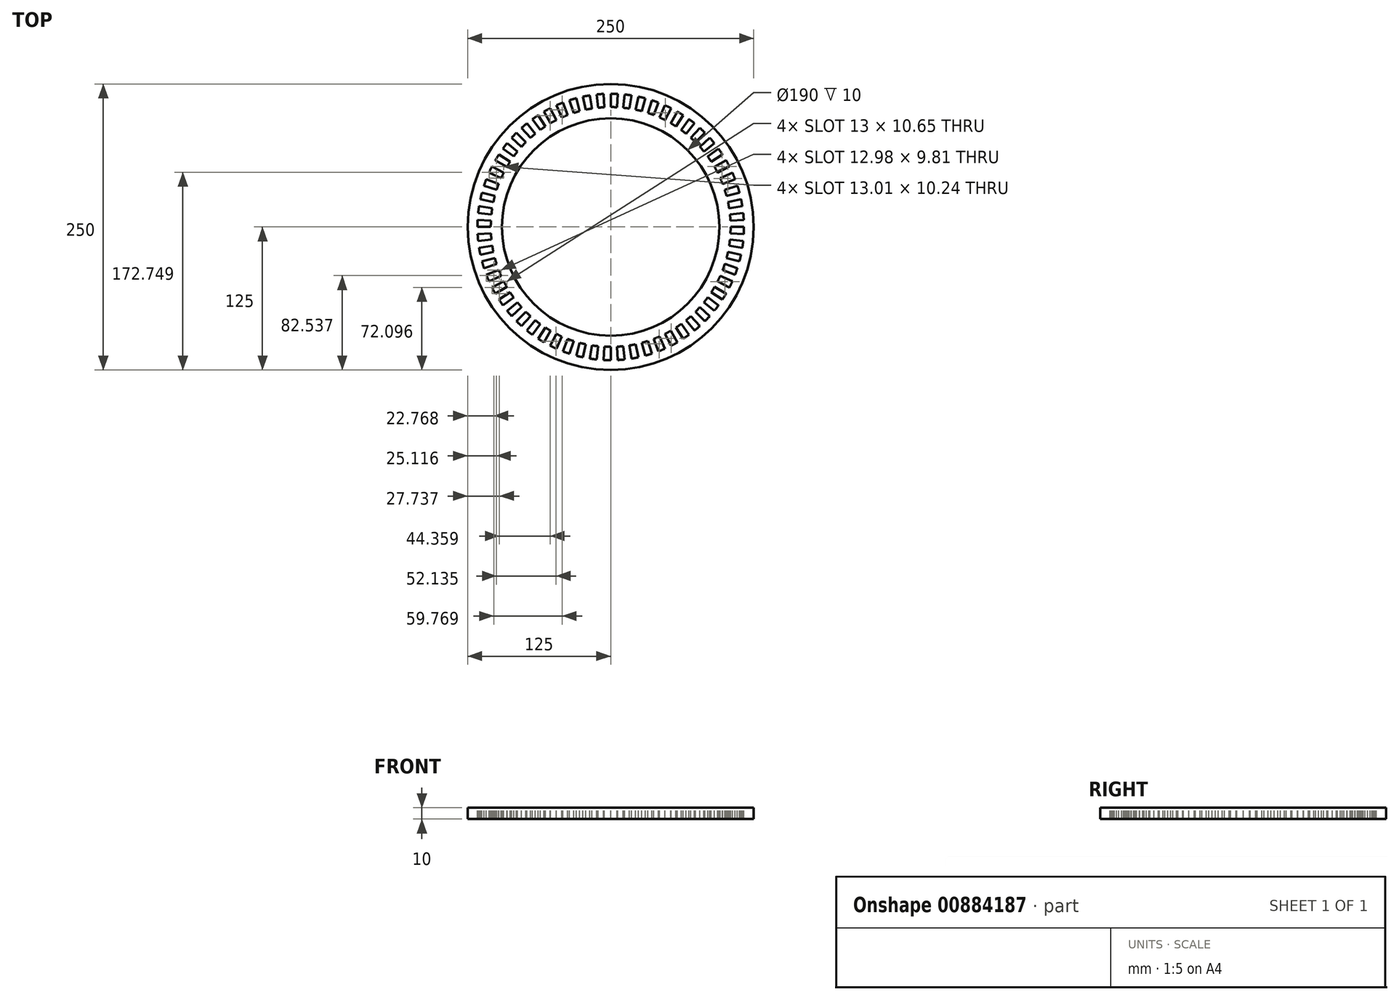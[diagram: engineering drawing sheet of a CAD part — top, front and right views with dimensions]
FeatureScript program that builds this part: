
annotation { "Feature Type Name" : "Feature", "Feature Type Description" : "" }
export const myFeature = defineFeature(function(context is Context, id is Id, definition is map)
    precondition{}
    {
        {
            var Q0;
            Q0=qCreatedBy(makeId("Top.planeOp"),FACE);
            var sketch = newSketch(context, id + "F0", { "sketchPlane" : qUnion([Q0])});
            skCircle(sketch, "E0", {"center": v(0, 0) * mm, "radius": 145 * mm});
            skArc(sketch, "E1", {"start": v(9.54, 136.41) * mm, "mid": v(4.77, 136.66) * mm, "end": v(0, 136.75) * mm});
            skArc(sketch, "E2", {"start": v(8, 114.55) * mm, "mid": v(4, 114.76) * mm, "end": v(0, 114.83) * mm});
            skLineSegment(sketch, "E3", {"start": v(0, 0) * mm, "end": v(0, 38.61) * mm, "construction": true});
            skLineSegment(sketch, "E4", {"start": v(0, 38.61) * mm, "end": v(0, 0) * mm, "construction": true});
            skLineSegment(sketch, "E5", {"start": v(0, 0) * mm, "end": v(-47.77, 0) * mm, "construction": true});
            skLineSegment(sketch, "E6", {"start": v(0, 30) * mm, "end": v(-10, 30) * mm});
            skLineSegment(sketch, "E7", {"start": v(-10, 30) * mm, "end": v(-10, 10) * mm});
            skLineSegment(sketch, "E8", {"start": v(-10, 10) * mm, "end": v(-30, 10) * mm});
            skLineSegment(sketch, "E9", {"start": v(-30, 10) * mm, "end": v(-30, 0) * mm});
            skLineSegment(sketch, "E10.MirrorCS", {"start": v(-30, -10) * mm, "end": v(-30, 0) * mm});
            skLineSegment(sketch, "E11.MirrorCS", {"start": v(-10, -10) * mm, "end": v(-30, -10) * mm});
            skLineSegment(sketch, "E12.MirrorCS", {"start": v(-10, -30) * mm, "end": v(-10, -10) * mm});
            skLineSegment(sketch, "E13.MirrorCS", {"start": v(0, -30) * mm, "end": v(-10, -30) * mm});
            skLineSegment(sketch, "E14.MirrorCS", {"start": v(0, 30) * mm, "end": v(10, 30) * mm});
            skLineSegment(sketch, "E15.MirrorCS", {"start": v(10, 30) * mm, "end": v(10, 10) * mm});
            skLineSegment(sketch, "E16.MirrorCS", {"start": v(10, 10) * mm, "end": v(30, 10) * mm});
            skLineSegment(sketch, "E17.MirrorCS", {"start": v(30, 10) * mm, "end": v(30, 0) * mm});
            skLineSegment(sketch, "E18.MirrorCS", {"start": v(30, -10) * mm, "end": v(30, 0) * mm});
            skLineSegment(sketch, "E19.MirrorCS", {"start": v(10, -10) * mm, "end": v(30, -10) * mm});
            skLineSegment(sketch, "E20.MirrorCS", {"start": v(0, -30) * mm, "end": v(10, -30) * mm});
            skLineSegment(sketch, "E21.MirrorCS", {"start": v(10, -30) * mm, "end": v(10, -10) * mm});
            skLineSegment(sketch, "E22", {"start": v(0, 114.83) * mm, "end": v(0, 136.75) * mm});
            skLineSegment(sketch, "E23", {"start": v(8, 114.55) * mm, "end": v(9.54, 136.41) * mm});
            skArc(sketch, "E24.1.0", {"start": v(-10, 114.4) * mm, "mid": v(-14, 113.98) * mm, "end": v(-17.96, 113.42) * mm});
            skLineSegment(sketch, "E24.1.1", {"start": v(-17.96, 113.42) * mm, "end": v(-21.4, 135.06) * mm});
            skArc(sketch, "E24.1.2", {"start": v(-11.92, 136.23) * mm, "mid": v(-16.67, 135.73) * mm, "end": v(-21.4, 135.06) * mm});
            skLineSegment(sketch, "E24.1.3", {"start": v(-10, 114.4) * mm, "end": v(-11.92, 136.23) * mm});
            skArc(sketch, "E24.2.0", {"start": v(-27.78, 111.42) * mm, "mid": v(-31.65, 110.39) * mm, "end": v(-35.49, 109.21) * mm});
            skLineSegment(sketch, "E24.2.1", {"start": v(-35.49, 109.21) * mm, "end": v(-42.26, 130.05) * mm});
            skArc(sketch, "E24.2.2", {"start": v(-33.08, 132.68) * mm, "mid": v(-37.7, 131.45) * mm, "end": v(-42.26, 130.05) * mm});
            skLineSegment(sketch, "E24.2.3", {"start": v(-27.78, 111.42) * mm, "end": v(-33.08, 132.68) * mm});
            skArc(sketch, "E24.3.0", {"start": v(-44.87, 105.7) * mm, "mid": v(-48.53, 104.07) * mm, "end": v(-52.13, 102.32) * mm});
            skLineSegment(sketch, "E24.3.1", {"start": v(-52.13, 102.32) * mm, "end": v(-62.08, 121.84) * mm});
            skArc(sketch, "E24.3.2", {"start": v(-53.43, 125.88) * mm, "mid": v(-57.8, 123.93) * mm, "end": v(-62.08, 121.84) * mm});
            skLineSegment(sketch, "E24.3.3", {"start": v(-44.87, 105.7) * mm, "end": v(-53.43, 125.88) * mm});
            skArc(sketch, "E24.4.0", {"start": v(-60.85, 97.38) * mm, "mid": v(-64.21, 95.2) * mm, "end": v(-67.5, 92.9) * mm});
            skLineSegment(sketch, "E24.4.1", {"start": v(-67.5, 92.9) * mm, "end": v(-80.38, 110.63) * mm});
            skArc(sketch, "E24.4.2", {"start": v(-72.47, 115.97) * mm, "mid": v(-76.47, 113.37) * mm, "end": v(-80.38, 110.63) * mm});
            skLineSegment(sketch, "E24.4.3", {"start": v(-60.85, 97.38) * mm, "end": v(-72.47, 115.97) * mm});
            skArc(sketch, "E24.5.0", {"start": v(-75.34, 86.67) * mm, "mid": v(-78.32, 83.98) * mm, "end": v(-81.2, 81.2) * mm});
            skLineSegment(sketch, "E24.5.1", {"start": v(-81.2, 81.2) * mm, "end": v(-96.7, 96.7) * mm});
            skArc(sketch, "E24.5.2", {"start": v(-89.71, 103.2) * mm, "mid": v(-93.26, 100.01) * mm, "end": v(-96.7, 96.7) * mm});
            skLineSegment(sketch, "E24.5.3", {"start": v(-75.34, 86.67) * mm, "end": v(-89.71, 103.2) * mm});
            skArc(sketch, "E24.6.0", {"start": v(-87.97, 73.81) * mm, "mid": v(-90.5, 70.7) * mm, "end": v(-92.9, 67.5) * mm});
            skLineSegment(sketch, "E24.6.1", {"start": v(-92.9, 67.5) * mm, "end": v(-110.63, 80.38) * mm});
            skArc(sketch, "E24.6.2", {"start": v(-104.75, 87.9) * mm, "mid": v(-107.76, 84.19) * mm, "end": v(-110.63, 80.38) * mm});
            skLineSegment(sketch, "E24.6.3", {"start": v(-87.97, 73.81) * mm, "end": v(-104.75, 87.9) * mm});
            skArc(sketch, "E24.7.0", {"start": v(-98.43, 59.14) * mm, "mid": v(-100.44, 55.67) * mm, "end": v(-102.32, 52.13) * mm});
            skLineSegment(sketch, "E24.7.1", {"start": v(-102.32, 52.13) * mm, "end": v(-121.84, 62.08) * mm});
            skArc(sketch, "E24.7.2", {"start": v(-117.22, 70.43) * mm, "mid": v(-119.6, 66.3) * mm, "end": v(-121.84, 62.08) * mm});
            skLineSegment(sketch, "E24.7.3", {"start": v(-98.43, 59.14) * mm, "end": v(-117.22, 70.43) * mm});
            skArc(sketch, "E24.8.0", {"start": v(-106.47, 43.02) * mm, "mid": v(-107.9, 39.28) * mm, "end": v(-109.21, 35.49) * mm});
            skLineSegment(sketch, "E24.8.1", {"start": v(-109.21, 35.49) * mm, "end": v(-130.05, 42.26) * mm});
            skArc(sketch, "E24.8.2", {"start": v(-126.79, 51.23) * mm, "mid": v(-128.5, 46.77) * mm, "end": v(-130.05, 42.26) * mm});
            skLineSegment(sketch, "E24.8.3", {"start": v(-106.47, 43.02) * mm, "end": v(-126.79, 51.23) * mm});
            skArc(sketch, "E24.9.0", {"start": v(-111.9, 25.83) * mm, "mid": v(-112.72, 21.91) * mm, "end": v(-113.42, 17.96) * mm});
            skLineSegment(sketch, "E24.9.1", {"start": v(-113.42, 17.96) * mm, "end": v(-135.06, 21.4) * mm});
            skArc(sketch, "E24.9.2", {"start": v(-133.24, 30.76) * mm, "mid": v(-134.23, 26.1) * mm, "end": v(-135.06, 21.4) * mm});
            skLineSegment(sketch, "E24.9.3", {"start": v(-111.9, 25.83) * mm, "end": v(-133.24, 30.76) * mm});
            skArc(sketch, "E24.10.0", {"start": v(-114.55, 8) * mm, "mid": v(-114.76, 4) * mm, "end": v(-114.83, 0) * mm});
            skLineSegment(sketch, "E24.10.1", {"start": v(-114.83, 0) * mm, "end": v(-136.75, 0) * mm});
            skArc(sketch, "E24.10.2", {"start": v(-136.41, 9.54) * mm, "mid": v(-136.66, 4.77) * mm, "end": v(-136.75, 0) * mm});
            skLineSegment(sketch, "E24.10.3", {"start": v(-114.55, 8) * mm, "end": v(-136.41, 9.54) * mm});
            skArc(sketch, "E24.11.0", {"start": v(-114.4, -10) * mm, "mid": v(-113.98, -14) * mm, "end": v(-113.42, -17.96) * mm});
            skLineSegment(sketch, "E24.11.1", {"start": v(-113.42, -17.96) * mm, "end": v(-135.06, -21.4) * mm});
            skArc(sketch, "E24.11.2", {"start": v(-136.23, -11.92) * mm, "mid": v(-135.73, -16.67) * mm, "end": v(-135.06, -21.4) * mm});
            skLineSegment(sketch, "E24.11.3", {"start": v(-114.4, -10) * mm, "end": v(-136.23, -11.92) * mm});
            skArc(sketch, "E24.12.0", {"start": v(-111.42, -27.78) * mm, "mid": v(-110.39, -31.65) * mm, "end": v(-109.21, -35.49) * mm});
            skLineSegment(sketch, "E24.12.1", {"start": v(-109.21, -35.49) * mm, "end": v(-130.05, -42.26) * mm});
            skArc(sketch, "E24.12.2", {"start": v(-132.68, -33.08) * mm, "mid": v(-131.45, -37.7) * mm, "end": v(-130.05, -42.26) * mm});
            skLineSegment(sketch, "E24.12.3", {"start": v(-111.42, -27.78) * mm, "end": v(-132.68, -33.08) * mm});
            skArc(sketch, "E24.13.0", {"start": v(-105.7, -44.87) * mm, "mid": v(-104.07, -48.53) * mm, "end": v(-102.32, -52.13) * mm});
            skLineSegment(sketch, "E24.13.1", {"start": v(-102.32, -52.13) * mm, "end": v(-121.84, -62.08) * mm});
            skArc(sketch, "E24.13.2", {"start": v(-125.88, -53.43) * mm, "mid": v(-123.93, -57.8) * mm, "end": v(-121.84, -62.08) * mm});
            skLineSegment(sketch, "E24.13.3", {"start": v(-105.7, -44.87) * mm, "end": v(-125.88, -53.43) * mm});
            skArc(sketch, "E24.14.0", {"start": v(-97.38, -60.85) * mm, "mid": v(-95.2, -64.21) * mm, "end": v(-92.9, -67.5) * mm});
            skLineSegment(sketch, "E24.14.1", {"start": v(-92.9, -67.5) * mm, "end": v(-110.63, -80.38) * mm});
            skArc(sketch, "E24.14.2", {"start": v(-115.97, -72.47) * mm, "mid": v(-113.37, -76.47) * mm, "end": v(-110.63, -80.38) * mm});
            skLineSegment(sketch, "E24.14.3", {"start": v(-97.38, -60.85) * mm, "end": v(-115.97, -72.47) * mm});
            skArc(sketch, "E24.15.0", {"start": v(-86.67, -75.34) * mm, "mid": v(-83.98, -78.32) * mm, "end": v(-81.2, -81.2) * mm});
            skLineSegment(sketch, "E24.15.1", {"start": v(-81.2, -81.2) * mm, "end": v(-96.7, -96.7) * mm});
            skArc(sketch, "E24.15.2", {"start": v(-103.2, -89.71) * mm, "mid": v(-100.01, -93.26) * mm, "end": v(-96.7, -96.7) * mm});
            skLineSegment(sketch, "E24.15.3", {"start": v(-86.67, -75.34) * mm, "end": v(-103.2, -89.71) * mm});
            skArc(sketch, "E24.16.0", {"start": v(-73.81, -87.97) * mm, "mid": v(-70.7, -90.5) * mm, "end": v(-67.5, -92.9) * mm});
            skLineSegment(sketch, "E24.16.1", {"start": v(-67.5, -92.9) * mm, "end": v(-80.38, -110.63) * mm});
            skArc(sketch, "E24.16.2", {"start": v(-87.9, -104.75) * mm, "mid": v(-84.19, -107.76) * mm, "end": v(-80.38, -110.63) * mm});
            skLineSegment(sketch, "E24.16.3", {"start": v(-73.81, -87.97) * mm, "end": v(-87.9, -104.75) * mm});
            skArc(sketch, "E24.17.0", {"start": v(-59.14, -98.43) * mm, "mid": v(-55.67, -100.44) * mm, "end": v(-52.13, -102.32) * mm});
            skLineSegment(sketch, "E24.17.1", {"start": v(-52.13, -102.32) * mm, "end": v(-62.08, -121.84) * mm});
            skArc(sketch, "E24.17.2", {"start": v(-70.43, -117.22) * mm, "mid": v(-66.3, -119.6) * mm, "end": v(-62.08, -121.84) * mm});
            skLineSegment(sketch, "E24.17.3", {"start": v(-59.14, -98.43) * mm, "end": v(-70.43, -117.22) * mm});
            skArc(sketch, "E24.18.0", {"start": v(-43.02, -106.47) * mm, "mid": v(-39.28, -107.9) * mm, "end": v(-35.49, -109.21) * mm});
            skLineSegment(sketch, "E24.18.1", {"start": v(-35.49, -109.21) * mm, "end": v(-42.26, -130.05) * mm});
            skArc(sketch, "E24.18.2", {"start": v(-51.23, -126.79) * mm, "mid": v(-46.77, -128.5) * mm, "end": v(-42.26, -130.05) * mm});
            skLineSegment(sketch, "E24.18.3", {"start": v(-43.02, -106.47) * mm, "end": v(-51.23, -126.79) * mm});
            skArc(sketch, "E24.19.0", {"start": v(-25.83, -111.9) * mm, "mid": v(-21.91, -112.72) * mm, "end": v(-17.96, -113.42) * mm});
            skLineSegment(sketch, "E24.19.1", {"start": v(-17.96, -113.42) * mm, "end": v(-21.4, -135.06) * mm});
            skArc(sketch, "E24.19.2", {"start": v(-30.76, -133.24) * mm, "mid": v(-26.1, -134.23) * mm, "end": v(-21.4, -135.06) * mm});
            skLineSegment(sketch, "E24.19.3", {"start": v(-25.83, -111.9) * mm, "end": v(-30.76, -133.24) * mm});
            skArc(sketch, "E24.20.0", {"start": v(-8, -114.55) * mm, "mid": v(-4, -114.76) * mm, "end": v(0, -114.83) * mm});
            skLineSegment(sketch, "E24.20.1", {"start": v(0, -114.83) * mm, "end": v(0, -136.75) * mm});
            skArc(sketch, "E24.20.2", {"start": v(-9.54, -136.41) * mm, "mid": v(-4.77, -136.66) * mm, "end": v(0, -136.75) * mm});
            skLineSegment(sketch, "E24.20.3", {"start": v(-8, -114.55) * mm, "end": v(-9.54, -136.41) * mm});
            skArc(sketch, "E24.21.0", {"start": v(10, -114.4) * mm, "mid": v(14, -113.98) * mm, "end": v(17.96, -113.42) * mm});
            skLineSegment(sketch, "E24.21.1", {"start": v(17.96, -113.42) * mm, "end": v(21.4, -135.06) * mm});
            skArc(sketch, "E24.21.2", {"start": v(11.92, -136.23) * mm, "mid": v(16.67, -135.73) * mm, "end": v(21.4, -135.06) * mm});
            skLineSegment(sketch, "E24.21.3", {"start": v(10, -114.4) * mm, "end": v(11.92, -136.23) * mm});
            skArc(sketch, "E24.22.0", {"start": v(27.78, -111.42) * mm, "mid": v(31.65, -110.39) * mm, "end": v(35.49, -109.21) * mm});
            skLineSegment(sketch, "E24.22.1", {"start": v(35.49, -109.21) * mm, "end": v(42.26, -130.05) * mm});
            skArc(sketch, "E24.22.2", {"start": v(33.08, -132.68) * mm, "mid": v(37.7, -131.45) * mm, "end": v(42.26, -130.05) * mm});
            skLineSegment(sketch, "E24.22.3", {"start": v(27.78, -111.42) * mm, "end": v(33.08, -132.68) * mm});
            skArc(sketch, "E24.23.0", {"start": v(44.87, -105.7) * mm, "mid": v(48.53, -104.07) * mm, "end": v(52.13, -102.32) * mm});
            skLineSegment(sketch, "E24.23.1", {"start": v(52.13, -102.32) * mm, "end": v(62.08, -121.84) * mm});
            skArc(sketch, "E24.23.2", {"start": v(53.43, -125.88) * mm, "mid": v(57.8, -123.93) * mm, "end": v(62.08, -121.84) * mm});
            skLineSegment(sketch, "E24.23.3", {"start": v(44.87, -105.7) * mm, "end": v(53.43, -125.88) * mm});
            skArc(sketch, "E24.24.0", {"start": v(60.85, -97.38) * mm, "mid": v(64.21, -95.2) * mm, "end": v(67.5, -92.9) * mm});
            skLineSegment(sketch, "E24.24.1", {"start": v(67.5, -92.9) * mm, "end": v(80.38, -110.63) * mm});
            skArc(sketch, "E24.24.2", {"start": v(72.47, -115.97) * mm, "mid": v(76.47, -113.37) * mm, "end": v(80.38, -110.63) * mm});
            skLineSegment(sketch, "E24.24.3", {"start": v(60.85, -97.38) * mm, "end": v(72.47, -115.97) * mm});
            skArc(sketch, "E24.25.0", {"start": v(75.34, -86.67) * mm, "mid": v(78.32, -83.98) * mm, "end": v(81.2, -81.2) * mm});
            skLineSegment(sketch, "E24.25.1", {"start": v(81.2, -81.2) * mm, "end": v(96.7, -96.7) * mm});
            skArc(sketch, "E24.25.2", {"start": v(89.71, -103.2) * mm, "mid": v(93.26, -100.01) * mm, "end": v(96.7, -96.7) * mm});
            skLineSegment(sketch, "E24.25.3", {"start": v(75.34, -86.67) * mm, "end": v(89.71, -103.2) * mm});
            skArc(sketch, "E24.26.0", {"start": v(87.97, -73.81) * mm, "mid": v(90.5, -70.7) * mm, "end": v(92.9, -67.5) * mm});
            skLineSegment(sketch, "E24.26.1", {"start": v(92.9, -67.5) * mm, "end": v(110.63, -80.38) * mm});
            skArc(sketch, "E24.26.2", {"start": v(104.75, -87.9) * mm, "mid": v(107.76, -84.19) * mm, "end": v(110.63, -80.38) * mm});
            skLineSegment(sketch, "E24.26.3", {"start": v(87.97, -73.81) * mm, "end": v(104.75, -87.9) * mm});
            skArc(sketch, "E24.27.0", {"start": v(98.43, -59.14) * mm, "mid": v(100.44, -55.67) * mm, "end": v(102.32, -52.13) * mm});
            skLineSegment(sketch, "E24.27.1", {"start": v(102.32, -52.13) * mm, "end": v(121.84, -62.08) * mm});
            skArc(sketch, "E24.27.2", {"start": v(117.22, -70.43) * mm, "mid": v(119.6, -66.3) * mm, "end": v(121.84, -62.08) * mm});
            skLineSegment(sketch, "E24.27.3", {"start": v(98.43, -59.14) * mm, "end": v(117.22, -70.43) * mm});
            skArc(sketch, "E24.28.0", {"start": v(106.47, -43.02) * mm, "mid": v(107.9, -39.28) * mm, "end": v(109.21, -35.49) * mm});
            skLineSegment(sketch, "E24.28.1", {"start": v(109.21, -35.49) * mm, "end": v(130.05, -42.26) * mm});
            skArc(sketch, "E24.28.2", {"start": v(126.79, -51.23) * mm, "mid": v(128.5, -46.77) * mm, "end": v(130.05, -42.26) * mm});
            skLineSegment(sketch, "E24.28.3", {"start": v(106.47, -43.02) * mm, "end": v(126.79, -51.23) * mm});
            skArc(sketch, "E24.29.0", {"start": v(111.9, -25.83) * mm, "mid": v(112.72, -21.91) * mm, "end": v(113.42, -17.96) * mm});
            skLineSegment(sketch, "E24.29.1", {"start": v(113.42, -17.96) * mm, "end": v(135.06, -21.4) * mm});
            skArc(sketch, "E24.29.2", {"start": v(133.24, -30.76) * mm, "mid": v(134.23, -26.1) * mm, "end": v(135.06, -21.4) * mm});
            skLineSegment(sketch, "E24.29.3", {"start": v(111.9, -25.83) * mm, "end": v(133.24, -30.76) * mm});
            skArc(sketch, "E24.30.0", {"start": v(114.55, -8) * mm, "mid": v(114.76, -4) * mm, "end": v(114.83, 0) * mm});
            skLineSegment(sketch, "E24.30.1", {"start": v(114.83, 0) * mm, "end": v(136.75, 0) * mm});
            skArc(sketch, "E24.30.2", {"start": v(136.41, -9.54) * mm, "mid": v(136.66, -4.77) * mm, "end": v(136.75, 0) * mm});
            skLineSegment(sketch, "E24.30.3", {"start": v(114.55, -8) * mm, "end": v(136.41, -9.54) * mm});
            skArc(sketch, "E24.31.0", {"start": v(114.4, 10) * mm, "mid": v(113.98, 14) * mm, "end": v(113.42, 17.96) * mm});
            skLineSegment(sketch, "E24.31.1", {"start": v(113.42, 17.96) * mm, "end": v(135.06, 21.4) * mm});
            skArc(sketch, "E24.31.2", {"start": v(136.23, 11.92) * mm, "mid": v(135.73, 16.67) * mm, "end": v(135.06, 21.4) * mm});
            skLineSegment(sketch, "E24.31.3", {"start": v(114.4, 10) * mm, "end": v(136.23, 11.92) * mm});
            skArc(sketch, "E24.32.0", {"start": v(111.42, 27.78) * mm, "mid": v(110.39, 31.65) * mm, "end": v(109.21, 35.49) * mm});
            skLineSegment(sketch, "E24.32.1", {"start": v(109.21, 35.49) * mm, "end": v(130.05, 42.26) * mm});
            skArc(sketch, "E24.32.2", {"start": v(132.68, 33.08) * mm, "mid": v(131.45, 37.7) * mm, "end": v(130.05, 42.26) * mm});
            skLineSegment(sketch, "E24.32.3", {"start": v(111.42, 27.78) * mm, "end": v(132.68, 33.08) * mm});
            skArc(sketch, "E24.33.0", {"start": v(105.7, 44.87) * mm, "mid": v(104.07, 48.53) * mm, "end": v(102.32, 52.13) * mm});
            skLineSegment(sketch, "E24.33.1", {"start": v(102.32, 52.13) * mm, "end": v(121.84, 62.08) * mm});
            skArc(sketch, "E24.33.2", {"start": v(125.88, 53.43) * mm, "mid": v(123.93, 57.8) * mm, "end": v(121.84, 62.08) * mm});
            skLineSegment(sketch, "E24.33.3", {"start": v(105.7, 44.87) * mm, "end": v(125.88, 53.43) * mm});
            skArc(sketch, "E24.34.0", {"start": v(97.38, 60.85) * mm, "mid": v(95.2, 64.21) * mm, "end": v(92.9, 67.5) * mm});
            skLineSegment(sketch, "E24.34.1", {"start": v(92.9, 67.5) * mm, "end": v(110.63, 80.38) * mm});
            skArc(sketch, "E24.34.2", {"start": v(115.97, 72.47) * mm, "mid": v(113.37, 76.47) * mm, "end": v(110.63, 80.38) * mm});
            skLineSegment(sketch, "E24.34.3", {"start": v(97.38, 60.85) * mm, "end": v(115.97, 72.47) * mm});
            skArc(sketch, "E24.35.0", {"start": v(86.67, 75.34) * mm, "mid": v(83.98, 78.32) * mm, "end": v(81.2, 81.2) * mm});
            skLineSegment(sketch, "E24.35.1", {"start": v(81.2, 81.2) * mm, "end": v(96.7, 96.7) * mm});
            skArc(sketch, "E24.35.2", {"start": v(103.2, 89.71) * mm, "mid": v(100.01, 93.26) * mm, "end": v(96.7, 96.7) * mm});
            skLineSegment(sketch, "E24.35.3", {"start": v(86.67, 75.34) * mm, "end": v(103.2, 89.71) * mm});
            skArc(sketch, "E24.36.0", {"start": v(73.81, 87.97) * mm, "mid": v(70.7, 90.5) * mm, "end": v(67.5, 92.9) * mm});
            skLineSegment(sketch, "E24.36.1", {"start": v(67.5, 92.9) * mm, "end": v(80.38, 110.63) * mm});
            skArc(sketch, "E24.36.2", {"start": v(87.9, 104.75) * mm, "mid": v(84.19, 107.76) * mm, "end": v(80.38, 110.63) * mm});
            skLineSegment(sketch, "E24.36.3", {"start": v(73.81, 87.97) * mm, "end": v(87.9, 104.75) * mm});
            skArc(sketch, "E24.37.0", {"start": v(59.14, 98.43) * mm, "mid": v(55.67, 100.44) * mm, "end": v(52.13, 102.32) * mm});
            skLineSegment(sketch, "E24.37.1", {"start": v(52.13, 102.32) * mm, "end": v(62.08, 121.84) * mm});
            skArc(sketch, "E24.37.2", {"start": v(70.43, 117.22) * mm, "mid": v(66.3, 119.6) * mm, "end": v(62.08, 121.84) * mm});
            skLineSegment(sketch, "E24.37.3", {"start": v(59.14, 98.43) * mm, "end": v(70.43, 117.22) * mm});
            skArc(sketch, "E24.38.0", {"start": v(43.02, 106.47) * mm, "mid": v(39.28, 107.9) * mm, "end": v(35.49, 109.21) * mm});
            skLineSegment(sketch, "E24.38.1", {"start": v(35.49, 109.21) * mm, "end": v(42.26, 130.05) * mm});
            skArc(sketch, "E24.38.2", {"start": v(51.23, 126.79) * mm, "mid": v(46.77, 128.5) * mm, "end": v(42.26, 130.05) * mm});
            skLineSegment(sketch, "E24.38.3", {"start": v(43.02, 106.47) * mm, "end": v(51.23, 126.79) * mm});
            skArc(sketch, "E24.39.0", {"start": v(25.83, 111.9) * mm, "mid": v(21.91, 112.72) * mm, "end": v(17.96, 113.42) * mm});
            skLineSegment(sketch, "E24.39.1", {"start": v(17.96, 113.42) * mm, "end": v(21.4, 135.06) * mm});
            skArc(sketch, "E24.39.2", {"start": v(30.76, 133.24) * mm, "mid": v(26.1, 134.23) * mm, "end": v(21.4, 135.06) * mm});
            skLineSegment(sketch, "E24.39.3", {"start": v(25.83, 111.9) * mm, "end": v(30.76, 133.24) * mm});
            skCircle(sketch, "E25", {"center": v(0, 0) * mm, "radius": 50 * mm});
            skSolve(sketch);
        }
        {
            var Q0;
            Q0=makeQuery(id+"F0.imprint","IMPRINT",FACE,{"disambiguationData":[TD([[makeQuery(id+"F0.imprint","IMPRINT",EDGE,{"derivedFrom":sQuery(id+"F0.wireOp",EDGE,"E6")}),-1.0]])]});
            extrude(context, id + "F1", {"entities" : qUnion([Q0]), "depth" : 10 * mm, "offsetDistance" : 25 * mm});
        }
        {
            var Q0;
            Q0=makeQuery(id+"F1.opExtrude","CAP_FACE",FACE,{"disambiguationData":[OSD([sQuery(id+"F0.wireOp",EDGE,"E6"),sQuery(id+"F0.wireOp",EDGE,"E7"),sQuery(id+"F0.wireOp",EDGE,"E8"),sQuery(id+"F0.wireOp",EDGE,"E9"),sQuery(id+"F0.wireOp",EDGE,"E10.MirrorCS"),sQuery(id+"F0.wireOp",EDGE,"E11.MirrorCS"),sQuery(id+"F0.wireOp",EDGE,"E12.MirrorCS"),sQuery(id+"F0.wireOp",EDGE,"E13.MirrorCS"),sQuery(id+"F0.wireOp",EDGE,"E14.MirrorCS"),sQuery(id+"F0.wireOp",EDGE,"E15.MirrorCS"),sQuery(id+"F0.wireOp",EDGE,"E16.MirrorCS"),sQuery(id+"F0.wireOp",EDGE,"E17.MirrorCS"),sQuery(id+"F0.wireOp",EDGE,"E18.MirrorCS"),sQuery(id+"F0.wireOp",EDGE,"E19.MirrorCS"),sQuery(id+"F0.wireOp",EDGE,"E20.MirrorCS"),sQuery(id+"F0.wireOp",EDGE,"E21.MirrorCS"),sQuery(id+"F0.wireOp",EDGE,"E25")])],"isStart":false});
            var sketch = newSketch(context, id + "F2", { "sketchPlane" : qUnion([Q0])});
            skCircle(sketch, "E26", {"center": v(0, 0) * mm, "radius": 125 * mm});
            skCircle(sketch, "E27", {"center": v(0, 0) * mm, "radius": 40.45 * mm});
            skSolve(sketch);
        }
        {
            var Q0;
            Q0=qSketchRegion(id+"F2",true);
            extrude(context, id + "F3", {"entities" : qUnion([Q0]), "operationType" : NewBodyOperationType.ADD, "oppositeDirection" : true, "depth" : 10 * mm, "offsetDistance" : 25 * mm});
        }
        {
            var Q0;
            Q0=makeQuery(id+"F3.boolean.opBoolean","MERGE",FACE,{"derivedFrom":[makeQuery(id+"F1.opExtrude","CAP_FACE",FACE,{"disambiguationData":[OSD([sQuery(id+"F0.wireOp",EDGE,"E6"),sQuery(id+"F0.wireOp",EDGE,"E7"),sQuery(id+"F0.wireOp",EDGE,"E8"),sQuery(id+"F0.wireOp",EDGE,"E9"),sQuery(id+"F0.wireOp",EDGE,"E10.MirrorCS"),sQuery(id+"F0.wireOp",EDGE,"E11.MirrorCS"),sQuery(id+"F0.wireOp",EDGE,"E12.MirrorCS"),sQuery(id+"F0.wireOp",EDGE,"E13.MirrorCS"),sQuery(id+"F0.wireOp",EDGE,"E14.MirrorCS"),sQuery(id+"F0.wireOp",EDGE,"E15.MirrorCS"),sQuery(id+"F0.wireOp",EDGE,"E16.MirrorCS"),sQuery(id+"F0.wireOp",EDGE,"E17.MirrorCS"),sQuery(id+"F0.wireOp",EDGE,"E18.MirrorCS"),sQuery(id+"F0.wireOp",EDGE,"E19.MirrorCS"),sQuery(id+"F0.wireOp",EDGE,"E20.MirrorCS"),sQuery(id+"F0.wireOp",EDGE,"E21.MirrorCS"),sQuery(id+"F0.wireOp",EDGE,"E25")])],"isStart":false}),makeQuery(id+"F3.opExtrude","CAP_FACE",FACE,{"disambiguationData":[OSD([sQuery(id+"F2.wireOp",EDGE,"E26"),sQuery(id+"F2.wireOp",EDGE,"E27")])],"isStart":true})]});
            var sketch = newSketch(context, id + "F4", { "sketchPlane" : qUnion([Q0])});
            skLineSegment(sketch, "E28", {"start": v(0, 104.8) * mm, "end": v(0, 116.46) * mm});
            skLineSegment(sketch, "E29", {"start": v(0, 116.46) * mm, "end": v(0, 104.8) * mm});
            skLineSegment(sketch, "E30", {"start": v(5.48, 104.66) * mm, "end": v(6.1, 116.3) * mm});
            skArc(sketch, "E31", {"start": v(6.1, 116.3) * mm, "mid": v(3.05, 116.42) * mm, "end": v(0, 116.46) * mm});
            skArc(sketch, "E32", {"start": v(5.48, 104.66) * mm, "mid": v(2.74, 104.77) * mm, "end": v(0, 104.8) * mm});
            skArc(sketch, "E33.1.0", {"start": v(-5.48, 104.66) * mm, "mid": v(-8.22, 104.48) * mm, "end": v(-10.95, 104.23) * mm});
            skLineSegment(sketch, "E33.1.1", {"start": v(-12.17, 115.82) * mm, "end": v(-10.95, 104.23) * mm});
            skArc(sketch, "E33.1.2", {"start": v(-6.1, 116.3) * mm, "mid": v(-9.14, 116.1) * mm, "end": v(-12.17, 115.82) * mm});
            skLineSegment(sketch, "E33.1.3", {"start": v(-5.48, 104.66) * mm, "end": v(-6.1, 116.3) * mm});
            skArc(sketch, "E33.2.0", {"start": v(-16.4, 103.51) * mm, "mid": v(-19.1, 103.05) * mm, "end": v(-21.79, 102.51) * mm});
            skLineSegment(sketch, "E33.2.1", {"start": v(-24.21, 113.91) * mm, "end": v(-21.79, 102.51) * mm});
            skArc(sketch, "E33.2.2", {"start": v(-18.22, 115.02) * mm, "mid": v(-21.22, 114.5) * mm, "end": v(-24.21, 113.91) * mm});
            skLineSegment(sketch, "E33.2.3", {"start": v(-16.4, 103.51) * mm, "end": v(-18.22, 115.02) * mm});
            skArc(sketch, "E33.3.0", {"start": v(-27.12, 101.23) * mm, "mid": v(-29.77, 100.49) * mm, "end": v(-32.39, 99.67) * mm});
            skLineSegment(sketch, "E33.3.1", {"start": v(-35.99, 110.76) * mm, "end": v(-32.39, 99.67) * mm});
            skArc(sketch, "E33.3.2", {"start": v(-30.14, 112.49) * mm, "mid": v(-33.08, 111.66) * mm, "end": v(-35.99, 110.76) * mm});
            skLineSegment(sketch, "E33.3.3", {"start": v(-27.12, 101.23) * mm, "end": v(-30.14, 112.49) * mm});
            skArc(sketch, "E33.4.0", {"start": v(-37.56, 97.84) * mm, "mid": v(-40.1, 96.83) * mm, "end": v(-42.63, 95.74) * mm});
            skLineSegment(sketch, "E33.4.1", {"start": v(-47.37, 106.39) * mm, "end": v(-42.63, 95.74) * mm});
            skArc(sketch, "E33.4.2", {"start": v(-41.73, 108.72) * mm, "mid": v(-44.57, 107.6) * mm, "end": v(-47.37, 106.39) * mm});
            skLineSegment(sketch, "E33.4.3", {"start": v(-37.56, 97.84) * mm, "end": v(-41.73, 108.72) * mm});
            skArc(sketch, "E33.5.0", {"start": v(-47.58, 93.38) * mm, "mid": v(-50, 92.1) * mm, "end": v(-52.4, 90.76) * mm});
            skLineSegment(sketch, "E33.5.1", {"start": v(-58.23, 100.85) * mm, "end": v(-52.4, 90.76) * mm});
            skArc(sketch, "E33.5.2", {"start": v(-52.87, 103.76) * mm, "mid": v(-55.57, 102.34) * mm, "end": v(-58.23, 100.85) * mm});
            skLineSegment(sketch, "E33.5.3", {"start": v(-47.58, 93.38) * mm, "end": v(-52.87, 103.76) * mm});
            skArc(sketch, "E33.6.0", {"start": v(-57.08, 87.9) * mm, "mid": v(-59.36, 86.37) * mm, "end": v(-61.6, 84.79) * mm});
            skLineSegment(sketch, "E33.6.1", {"start": v(-68.45, 94.22) * mm, "end": v(-61.6, 84.79) * mm});
            skArc(sketch, "E33.6.2", {"start": v(-63.43, 97.67) * mm, "mid": v(-65.96, 95.97) * mm, "end": v(-68.45, 94.22) * mm});
            skLineSegment(sketch, "E33.6.3", {"start": v(-57.08, 87.9) * mm, "end": v(-63.43, 97.67) * mm});
            skArc(sketch, "E33.7.0", {"start": v(-65.95, 81.45) * mm, "mid": v(-68.06, 79.7) * mm, "end": v(-70.13, 77.88) * mm});
            skLineSegment(sketch, "E33.7.1", {"start": v(-77.92, 86.54) * mm, "end": v(-70.13, 77.88) * mm});
            skArc(sketch, "E33.7.2", {"start": v(-73.29, 90.5) * mm, "mid": v(-75.63, 88.55) * mm, "end": v(-77.92, 86.54) * mm});
            skLineSegment(sketch, "E33.7.3", {"start": v(-65.95, 81.45) * mm, "end": v(-73.29, 90.5) * mm});
            skArc(sketch, "E33.8.0", {"start": v(-74.1, 74.1) * mm, "mid": v(-76.02, 72.14) * mm, "end": v(-77.88, 70.13) * mm});
            skLineSegment(sketch, "E33.8.1", {"start": v(-86.54, 77.92) * mm, "end": v(-77.88, 70.13) * mm});
            skArc(sketch, "E33.8.2", {"start": v(-82.35, 82.35) * mm, "mid": v(-84.47, 80.16) * mm, "end": v(-86.54, 77.92) * mm});
            skLineSegment(sketch, "E33.8.3", {"start": v(-74.1, 74.1) * mm, "end": v(-82.35, 82.35) * mm});
            skArc(sketch, "E33.9.0", {"start": v(-81.45, 65.95) * mm, "mid": v(-83.15, 63.8) * mm, "end": v(-84.79, 61.6) * mm});
            skLineSegment(sketch, "E33.9.1", {"start": v(-94.22, 68.45) * mm, "end": v(-84.79, 61.6) * mm});
            skArc(sketch, "E33.9.2", {"start": v(-90.5, 73.29) * mm, "mid": v(-92.4, 70.9) * mm, "end": v(-94.22, 68.45) * mm});
            skLineSegment(sketch, "E33.9.3", {"start": v(-81.45, 65.95) * mm, "end": v(-90.5, 73.29) * mm});
            skArc(sketch, "E33.10.0", {"start": v(-87.9, 57.08) * mm, "mid": v(-89.36, 54.76) * mm, "end": v(-90.76, 52.4) * mm});
            skLineSegment(sketch, "E33.10.1", {"start": v(-100.85, 58.23) * mm, "end": v(-90.76, 52.4) * mm});
            skArc(sketch, "E33.10.2", {"start": v(-97.67, 63.43) * mm, "mid": v(-99.3, 60.85) * mm, "end": v(-100.85, 58.23) * mm});
            skLineSegment(sketch, "E33.10.3", {"start": v(-87.9, 57.08) * mm, "end": v(-97.67, 63.43) * mm});
            skArc(sketch, "E33.11.0", {"start": v(-93.38, 47.58) * mm, "mid": v(-94.6, 45.12) * mm, "end": v(-95.74, 42.63) * mm});
            skLineSegment(sketch, "E33.11.1", {"start": v(-106.39, 47.37) * mm, "end": v(-95.74, 42.63) * mm});
            skArc(sketch, "E33.11.2", {"start": v(-103.76, 52.87) * mm, "mid": v(-105.11, 50.14) * mm, "end": v(-106.39, 47.37) * mm});
            skLineSegment(sketch, "E33.11.3", {"start": v(-93.38, 47.58) * mm, "end": v(-103.76, 52.87) * mm});
            skArc(sketch, "E33.12.0", {"start": v(-97.84, 37.56) * mm, "mid": v(-98.8, 34.98) * mm, "end": v(-99.67, 32.39) * mm});
            skLineSegment(sketch, "E33.12.1", {"start": v(-110.76, 35.99) * mm, "end": v(-99.67, 32.39) * mm});
            skArc(sketch, "E33.12.2", {"start": v(-108.72, 41.73) * mm, "mid": v(-109.78, 38.87) * mm, "end": v(-110.76, 35.99) * mm});
            skLineSegment(sketch, "E33.12.3", {"start": v(-97.84, 37.56) * mm, "end": v(-108.72, 41.73) * mm});
            skArc(sketch, "E33.13.0", {"start": v(-101.23, 27.12) * mm, "mid": v(-101.9, 24.47) * mm, "end": v(-102.51, 21.79) * mm});
            skLineSegment(sketch, "E33.13.1", {"start": v(-113.91, 24.21) * mm, "end": v(-102.51, 21.79) * mm});
            skArc(sketch, "E33.13.2", {"start": v(-112.49, 30.14) * mm, "mid": v(-113.24, 27.19) * mm, "end": v(-113.91, 24.21) * mm});
            skLineSegment(sketch, "E33.13.3", {"start": v(-101.23, 27.12) * mm, "end": v(-112.49, 30.14) * mm});
            skArc(sketch, "E33.14.0", {"start": v(-103.51, 16.4) * mm, "mid": v(-103.9, 13.68) * mm, "end": v(-104.23, 10.95) * mm});
            skLineSegment(sketch, "E33.14.1", {"start": v(-115.82, 12.17) * mm, "end": v(-104.23, 10.95) * mm});
            skArc(sketch, "E33.14.2", {"start": v(-115.02, 18.22) * mm, "mid": v(-115.46, 15.2) * mm, "end": v(-115.82, 12.17) * mm});
            skLineSegment(sketch, "E33.14.3", {"start": v(-103.51, 16.4) * mm, "end": v(-115.02, 18.22) * mm});
            skArc(sketch, "E33.15.0", {"start": v(-104.66, 5.48) * mm, "mid": v(-104.77, 2.74) * mm, "end": v(-104.8, 0) * mm});
            skLineSegment(sketch, "E33.15.1", {"start": v(-116.46, 0) * mm, "end": v(-104.8, 0) * mm});
            skArc(sketch, "E33.15.2", {"start": v(-116.3, 6.1) * mm, "mid": v(-116.42, 3.05) * mm, "end": v(-116.46, 0) * mm});
            skLineSegment(sketch, "E33.15.3", {"start": v(-104.66, 5.48) * mm, "end": v(-116.3, 6.1) * mm});
            skArc(sketch, "E33.16.0", {"start": v(-104.66, -5.48) * mm, "mid": v(-104.48, -8.22) * mm, "end": v(-104.23, -10.95) * mm});
            skLineSegment(sketch, "E33.16.1", {"start": v(-115.82, -12.17) * mm, "end": v(-104.23, -10.95) * mm});
            skArc(sketch, "E33.16.2", {"start": v(-116.3, -6.1) * mm, "mid": v(-116.1, -9.14) * mm, "end": v(-115.82, -12.17) * mm});
            skLineSegment(sketch, "E33.16.3", {"start": v(-104.66, -5.48) * mm, "end": v(-116.3, -6.1) * mm});
            skArc(sketch, "E33.17.0", {"start": v(-103.51, -16.4) * mm, "mid": v(-103.05, -19.1) * mm, "end": v(-102.51, -21.79) * mm});
            skLineSegment(sketch, "E33.17.1", {"start": v(-113.91, -24.21) * mm, "end": v(-102.51, -21.79) * mm});
            skArc(sketch, "E33.17.2", {"start": v(-115.02, -18.22) * mm, "mid": v(-114.5, -21.22) * mm, "end": v(-113.91, -24.21) * mm});
            skLineSegment(sketch, "E33.17.3", {"start": v(-103.51, -16.4) * mm, "end": v(-115.02, -18.22) * mm});
            skArc(sketch, "E34.3.18.0", {"start": v(-101.23, -27.12) * mm, "mid": v(-100.49, -29.77) * mm, "end": v(-99.67, -32.39) * mm});
            skLineSegment(sketch, "E34.4.18.0", {"start": v(-110.76, -35.99) * mm, "end": v(-99.67, -32.39) * mm});
            skArc(sketch, "E34.7.18.0", {"start": v(-112.49, -30.14) * mm, "mid": v(-111.66, -33.08) * mm, "end": v(-110.76, -35.99) * mm});
            skLineSegment(sketch, "E34.11.18.0", {"start": v(-101.23, -27.12) * mm, "end": v(-112.49, -30.14) * mm});
            skArc(sketch, "E34.3.19.0", {"start": v(-97.84, -37.56) * mm, "mid": v(-96.83, -40.1) * mm, "end": v(-95.74, -42.63) * mm});
            skLineSegment(sketch, "E34.4.19.0", {"start": v(-106.39, -47.37) * mm, "end": v(-95.74, -42.63) * mm});
            skArc(sketch, "E34.7.19.0", {"start": v(-108.72, -41.73) * mm, "mid": v(-107.6, -44.57) * mm, "end": v(-106.39, -47.37) * mm});
            skLineSegment(sketch, "E34.11.19.0", {"start": v(-97.84, -37.56) * mm, "end": v(-108.72, -41.73) * mm});
            skArc(sketch, "E34.3.20.0", {"start": v(-93.38, -47.58) * mm, "mid": v(-92.1, -50) * mm, "end": v(-90.76, -52.4) * mm});
            skLineSegment(sketch, "E34.4.20.0", {"start": v(-100.85, -58.23) * mm, "end": v(-90.76, -52.4) * mm});
            skArc(sketch, "E34.7.20.0", {"start": v(-103.76, -52.87) * mm, "mid": v(-102.34, -55.57) * mm, "end": v(-100.85, -58.23) * mm});
            skLineSegment(sketch, "E34.11.20.0", {"start": v(-93.38, -47.58) * mm, "end": v(-103.76, -52.87) * mm});
            skArc(sketch, "E34.3.21.0", {"start": v(-87.9, -57.08) * mm, "mid": v(-86.37, -59.36) * mm, "end": v(-84.79, -61.6) * mm});
            skLineSegment(sketch, "E34.4.21.0", {"start": v(-94.22, -68.45) * mm, "end": v(-84.79, -61.6) * mm});
            skArc(sketch, "E34.7.21.0", {"start": v(-97.67, -63.43) * mm, "mid": v(-95.97, -65.96) * mm, "end": v(-94.22, -68.45) * mm});
            skLineSegment(sketch, "E34.11.21.0", {"start": v(-87.9, -57.08) * mm, "end": v(-97.67, -63.43) * mm});
            skArc(sketch, "E34.3.22.0", {"start": v(-81.45, -65.95) * mm, "mid": v(-79.7, -68.06) * mm, "end": v(-77.88, -70.13) * mm});
            skLineSegment(sketch, "E34.4.22.0", {"start": v(-86.54, -77.92) * mm, "end": v(-77.88, -70.13) * mm});
            skArc(sketch, "E34.7.22.0", {"start": v(-90.5, -73.29) * mm, "mid": v(-88.55, -75.63) * mm, "end": v(-86.54, -77.92) * mm});
            skLineSegment(sketch, "E34.11.22.0", {"start": v(-81.45, -65.95) * mm, "end": v(-90.5, -73.29) * mm});
            skArc(sketch, "E34.3.23.0", {"start": v(-74.1, -74.1) * mm, "mid": v(-72.14, -76.02) * mm, "end": v(-70.13, -77.88) * mm});
            skLineSegment(sketch, "E34.4.23.0", {"start": v(-77.92, -86.54) * mm, "end": v(-70.13, -77.88) * mm});
            skArc(sketch, "E34.7.23.0", {"start": v(-82.35, -82.35) * mm, "mid": v(-80.16, -84.47) * mm, "end": v(-77.92, -86.54) * mm});
            skLineSegment(sketch, "E34.11.23.0", {"start": v(-74.1, -74.1) * mm, "end": v(-82.35, -82.35) * mm});
            skArc(sketch, "E34.3.24.0", {"start": v(-65.95, -81.45) * mm, "mid": v(-63.8, -83.15) * mm, "end": v(-61.6, -84.79) * mm});
            skLineSegment(sketch, "E34.4.24.0", {"start": v(-68.45, -94.22) * mm, "end": v(-61.6, -84.79) * mm});
            skArc(sketch, "E34.7.24.0", {"start": v(-73.29, -90.5) * mm, "mid": v(-70.9, -92.4) * mm, "end": v(-68.45, -94.22) * mm});
            skLineSegment(sketch, "E34.11.24.0", {"start": v(-65.95, -81.45) * mm, "end": v(-73.29, -90.5) * mm});
            skArc(sketch, "E34.3.25.0", {"start": v(-57.08, -87.9) * mm, "mid": v(-54.76, -89.36) * mm, "end": v(-52.4, -90.76) * mm});
            skLineSegment(sketch, "E34.4.25.0", {"start": v(-58.23, -100.85) * mm, "end": v(-52.4, -90.76) * mm});
            skArc(sketch, "E34.7.25.0", {"start": v(-63.43, -97.67) * mm, "mid": v(-60.85, -99.3) * mm, "end": v(-58.23, -100.85) * mm});
            skLineSegment(sketch, "E34.11.25.0", {"start": v(-57.08, -87.9) * mm, "end": v(-63.43, -97.67) * mm});
            skArc(sketch, "E34.3.26.0", {"start": v(-47.58, -93.38) * mm, "mid": v(-45.12, -94.6) * mm, "end": v(-42.63, -95.74) * mm});
            skLineSegment(sketch, "E34.4.26.0", {"start": v(-47.37, -106.39) * mm, "end": v(-42.63, -95.74) * mm});
            skArc(sketch, "E34.7.26.0", {"start": v(-52.87, -103.76) * mm, "mid": v(-50.14, -105.11) * mm, "end": v(-47.37, -106.39) * mm});
            skLineSegment(sketch, "E34.11.26.0", {"start": v(-47.58, -93.38) * mm, "end": v(-52.87, -103.76) * mm});
            skArc(sketch, "E34.3.27.0", {"start": v(-37.56, -97.84) * mm, "mid": v(-34.98, -98.8) * mm, "end": v(-32.39, -99.67) * mm});
            skLineSegment(sketch, "E34.4.27.0", {"start": v(-35.99, -110.76) * mm, "end": v(-32.39, -99.67) * mm});
            skArc(sketch, "E34.7.27.0", {"start": v(-41.73, -108.72) * mm, "mid": v(-38.87, -109.78) * mm, "end": v(-35.99, -110.76) * mm});
            skLineSegment(sketch, "E34.11.27.0", {"start": v(-37.56, -97.84) * mm, "end": v(-41.73, -108.72) * mm});
            skArc(sketch, "E34.3.28.0", {"start": v(-27.12, -101.23) * mm, "mid": v(-24.47, -101.9) * mm, "end": v(-21.79, -102.51) * mm});
            skLineSegment(sketch, "E34.4.28.0", {"start": v(-24.21, -113.91) * mm, "end": v(-21.79, -102.51) * mm});
            skArc(sketch, "E34.7.28.0", {"start": v(-30.14, -112.49) * mm, "mid": v(-27.19, -113.24) * mm, "end": v(-24.21, -113.91) * mm});
            skLineSegment(sketch, "E34.11.28.0", {"start": v(-27.12, -101.23) * mm, "end": v(-30.14, -112.49) * mm});
            skArc(sketch, "E34.3.29.0", {"start": v(-16.4, -103.51) * mm, "mid": v(-13.68, -103.9) * mm, "end": v(-10.95, -104.23) * mm});
            skLineSegment(sketch, "E34.4.29.0", {"start": v(-12.17, -115.82) * mm, "end": v(-10.95, -104.23) * mm});
            skArc(sketch, "E34.7.29.0", {"start": v(-18.22, -115.02) * mm, "mid": v(-15.2, -115.46) * mm, "end": v(-12.17, -115.82) * mm});
            skLineSegment(sketch, "E34.11.29.0", {"start": v(-16.4, -103.51) * mm, "end": v(-18.22, -115.02) * mm});
            skArc(sketch, "E34.3.30.0", {"start": v(-5.48, -104.66) * mm, "mid": v(-2.74, -104.77) * mm, "end": v(0, -104.8) * mm});
            skLineSegment(sketch, "E34.4.30.0", {"start": v(0, -116.46) * mm, "end": v(0, -104.8) * mm});
            skArc(sketch, "E34.7.30.0", {"start": v(-6.1, -116.3) * mm, "mid": v(-3.05, -116.42) * mm, "end": v(0, -116.46) * mm});
            skLineSegment(sketch, "E34.11.30.0", {"start": v(-5.48, -104.66) * mm, "end": v(-6.1, -116.3) * mm});
            skArc(sketch, "E34.3.31.0", {"start": v(5.48, -104.66) * mm, "mid": v(8.22, -104.48) * mm, "end": v(10.95, -104.23) * mm});
            skLineSegment(sketch, "E34.4.31.0", {"start": v(12.17, -115.82) * mm, "end": v(10.95, -104.23) * mm});
            skArc(sketch, "E34.7.31.0", {"start": v(6.1, -116.3) * mm, "mid": v(9.14, -116.1) * mm, "end": v(12.17, -115.82) * mm});
            skLineSegment(sketch, "E34.11.31.0", {"start": v(5.48, -104.66) * mm, "end": v(6.1, -116.3) * mm});
            skArc(sketch, "E34.3.32.0", {"start": v(16.4, -103.51) * mm, "mid": v(19.1, -103.05) * mm, "end": v(21.79, -102.51) * mm});
            skLineSegment(sketch, "E34.4.32.0", {"start": v(24.21, -113.91) * mm, "end": v(21.79, -102.51) * mm});
            skArc(sketch, "E34.7.32.0", {"start": v(18.22, -115.02) * mm, "mid": v(21.22, -114.5) * mm, "end": v(24.21, -113.91) * mm});
            skLineSegment(sketch, "E34.11.32.0", {"start": v(16.4, -103.51) * mm, "end": v(18.22, -115.02) * mm});
            skArc(sketch, "E34.3.33.0", {"start": v(27.12, -101.23) * mm, "mid": v(29.77, -100.49) * mm, "end": v(32.39, -99.67) * mm});
            skLineSegment(sketch, "E34.4.33.0", {"start": v(35.99, -110.76) * mm, "end": v(32.39, -99.67) * mm});
            skArc(sketch, "E34.7.33.0", {"start": v(30.14, -112.49) * mm, "mid": v(33.08, -111.66) * mm, "end": v(35.99, -110.76) * mm});
            skLineSegment(sketch, "E34.11.33.0", {"start": v(27.12, -101.23) * mm, "end": v(30.14, -112.49) * mm});
            skArc(sketch, "E34.3.34.0", {"start": v(37.56, -97.84) * mm, "mid": v(40.1, -96.83) * mm, "end": v(42.63, -95.74) * mm});
            skLineSegment(sketch, "E34.4.34.0", {"start": v(47.37, -106.39) * mm, "end": v(42.63, -95.74) * mm});
            skArc(sketch, "E34.7.34.0", {"start": v(41.73, -108.72) * mm, "mid": v(44.57, -107.6) * mm, "end": v(47.37, -106.39) * mm});
            skLineSegment(sketch, "E34.11.34.0", {"start": v(37.56, -97.84) * mm, "end": v(41.73, -108.72) * mm});
            skArc(sketch, "E34.3.35.0", {"start": v(47.58, -93.38) * mm, "mid": v(50, -92.1) * mm, "end": v(52.4, -90.76) * mm});
            skLineSegment(sketch, "E34.4.35.0", {"start": v(58.23, -100.85) * mm, "end": v(52.4, -90.76) * mm});
            skArc(sketch, "E34.7.35.0", {"start": v(52.87, -103.76) * mm, "mid": v(55.57, -102.34) * mm, "end": v(58.23, -100.85) * mm});
            skLineSegment(sketch, "E34.11.35.0", {"start": v(47.58, -93.38) * mm, "end": v(52.87, -103.76) * mm});
            skArc(sketch, "E35.3.36.0", {"start": v(57.08, -87.9) * mm, "mid": v(59.36, -86.37) * mm, "end": v(61.6, -84.79) * mm});
            skLineSegment(sketch, "E35.4.36.0", {"start": v(68.45, -94.22) * mm, "end": v(61.6, -84.79) * mm});
            skArc(sketch, "E35.7.36.0", {"start": v(63.43, -97.67) * mm, "mid": v(65.96, -95.97) * mm, "end": v(68.45, -94.22) * mm});
            skLineSegment(sketch, "E35.11.36.0", {"start": v(57.08, -87.9) * mm, "end": v(63.43, -97.67) * mm});
            skArc(sketch, "E35.3.37.0", {"start": v(65.95, -81.45) * mm, "mid": v(68.06, -79.7) * mm, "end": v(70.13, -77.88) * mm});
            skLineSegment(sketch, "E35.4.37.0", {"start": v(77.92, -86.54) * mm, "end": v(70.13, -77.88) * mm});
            skArc(sketch, "E35.7.37.0", {"start": v(73.29, -90.5) * mm, "mid": v(75.63, -88.55) * mm, "end": v(77.92, -86.54) * mm});
            skLineSegment(sketch, "E35.11.37.0", {"start": v(65.95, -81.45) * mm, "end": v(73.29, -90.5) * mm});
            skArc(sketch, "E35.3.38.0", {"start": v(74.1, -74.1) * mm, "mid": v(76.02, -72.14) * mm, "end": v(77.88, -70.13) * mm});
            skLineSegment(sketch, "E35.4.38.0", {"start": v(86.54, -77.92) * mm, "end": v(77.88, -70.13) * mm});
            skArc(sketch, "E35.7.38.0", {"start": v(82.35, -82.35) * mm, "mid": v(84.47, -80.16) * mm, "end": v(86.54, -77.92) * mm});
            skLineSegment(sketch, "E35.11.38.0", {"start": v(74.1, -74.1) * mm, "end": v(82.35, -82.35) * mm});
            skArc(sketch, "E35.3.39.0", {"start": v(81.45, -65.95) * mm, "mid": v(83.15, -63.8) * mm, "end": v(84.79, -61.6) * mm});
            skLineSegment(sketch, "E35.4.39.0", {"start": v(94.22, -68.45) * mm, "end": v(84.79, -61.6) * mm});
            skArc(sketch, "E35.7.39.0", {"start": v(90.5, -73.29) * mm, "mid": v(92.4, -70.9) * mm, "end": v(94.22, -68.45) * mm});
            skLineSegment(sketch, "E35.11.39.0", {"start": v(81.45, -65.95) * mm, "end": v(90.5, -73.29) * mm});
            skArc(sketch, "E35.3.40.0", {"start": v(87.9, -57.08) * mm, "mid": v(89.36, -54.76) * mm, "end": v(90.76, -52.4) * mm});
            skLineSegment(sketch, "E35.4.40.0", {"start": v(100.85, -58.23) * mm, "end": v(90.76, -52.4) * mm});
            skArc(sketch, "E35.7.40.0", {"start": v(97.67, -63.43) * mm, "mid": v(99.3, -60.85) * mm, "end": v(100.85, -58.23) * mm});
            skLineSegment(sketch, "E35.11.40.0", {"start": v(87.9, -57.08) * mm, "end": v(97.67, -63.43) * mm});
            skArc(sketch, "E35.3.41.0", {"start": v(93.38, -47.58) * mm, "mid": v(94.6, -45.12) * mm, "end": v(95.74, -42.63) * mm});
            skLineSegment(sketch, "E35.4.41.0", {"start": v(106.39, -47.37) * mm, "end": v(95.74, -42.63) * mm});
            skArc(sketch, "E35.7.41.0", {"start": v(103.76, -52.87) * mm, "mid": v(105.11, -50.14) * mm, "end": v(106.39, -47.37) * mm});
            skLineSegment(sketch, "E35.11.41.0", {"start": v(93.38, -47.58) * mm, "end": v(103.76, -52.87) * mm});
            skArc(sketch, "E35.3.42.0", {"start": v(97.84, -37.56) * mm, "mid": v(98.8, -34.98) * mm, "end": v(99.67, -32.39) * mm});
            skLineSegment(sketch, "E35.4.42.0", {"start": v(110.76, -35.99) * mm, "end": v(99.67, -32.39) * mm});
            skArc(sketch, "E35.7.42.0", {"start": v(108.72, -41.73) * mm, "mid": v(109.78, -38.87) * mm, "end": v(110.76, -35.99) * mm});
            skLineSegment(sketch, "E35.11.42.0", {"start": v(97.84, -37.56) * mm, "end": v(108.72, -41.73) * mm});
            skArc(sketch, "E35.3.43.0", {"start": v(101.23, -27.12) * mm, "mid": v(101.9, -24.47) * mm, "end": v(102.51, -21.79) * mm});
            skLineSegment(sketch, "E35.4.43.0", {"start": v(113.91, -24.21) * mm, "end": v(102.51, -21.79) * mm});
            skArc(sketch, "E35.7.43.0", {"start": v(112.49, -30.14) * mm, "mid": v(113.24, -27.19) * mm, "end": v(113.91, -24.21) * mm});
            skLineSegment(sketch, "E35.11.43.0", {"start": v(101.23, -27.12) * mm, "end": v(112.49, -30.14) * mm});
            skArc(sketch, "E35.3.44.0", {"start": v(103.51, -16.4) * mm, "mid": v(103.9, -13.68) * mm, "end": v(104.23, -10.95) * mm});
            skLineSegment(sketch, "E35.4.44.0", {"start": v(115.82, -12.17) * mm, "end": v(104.23, -10.95) * mm});
            skArc(sketch, "E35.7.44.0", {"start": v(115.02, -18.22) * mm, "mid": v(115.46, -15.2) * mm, "end": v(115.82, -12.17) * mm});
            skLineSegment(sketch, "E35.11.44.0", {"start": v(103.51, -16.4) * mm, "end": v(115.02, -18.22) * mm});
            skArc(sketch, "E36.3.45.0", {"start": v(104.66, -5.48) * mm, "mid": v(104.77, -2.74) * mm, "end": v(104.8, 0) * mm});
            skLineSegment(sketch, "E36.4.45.0", {"start": v(116.46, 0) * mm, "end": v(104.8, 0) * mm});
            skArc(sketch, "E36.7.45.0", {"start": v(116.3, -6.1) * mm, "mid": v(116.42, -3.05) * mm, "end": v(116.46, 0) * mm});
            skLineSegment(sketch, "E36.11.45.0", {"start": v(104.66, -5.48) * mm, "end": v(116.3, -6.1) * mm});
            skArc(sketch, "E36.3.46.0", {"start": v(104.66, 5.48) * mm, "mid": v(104.48, 8.22) * mm, "end": v(104.23, 10.95) * mm});
            skLineSegment(sketch, "E36.4.46.0", {"start": v(115.82, 12.17) * mm, "end": v(104.23, 10.95) * mm});
            skArc(sketch, "E36.7.46.0", {"start": v(116.3, 6.1) * mm, "mid": v(116.1, 9.14) * mm, "end": v(115.82, 12.17) * mm});
            skLineSegment(sketch, "E36.11.46.0", {"start": v(104.66, 5.48) * mm, "end": v(116.3, 6.1) * mm});
            skArc(sketch, "E36.3.47.0", {"start": v(103.51, 16.4) * mm, "mid": v(103.05, 19.1) * mm, "end": v(102.51, 21.79) * mm});
            skLineSegment(sketch, "E36.4.47.0", {"start": v(113.91, 24.21) * mm, "end": v(102.51, 21.79) * mm});
            skArc(sketch, "E36.7.47.0", {"start": v(115.02, 18.22) * mm, "mid": v(114.5, 21.22) * mm, "end": v(113.91, 24.21) * mm});
            skLineSegment(sketch, "E36.11.47.0", {"start": v(103.51, 16.4) * mm, "end": v(115.02, 18.22) * mm});
            skArc(sketch, "E36.3.48.0", {"start": v(101.23, 27.12) * mm, "mid": v(100.49, 29.77) * mm, "end": v(99.67, 32.39) * mm});
            skLineSegment(sketch, "E36.4.48.0", {"start": v(110.76, 35.99) * mm, "end": v(99.67, 32.39) * mm});
            skArc(sketch, "E36.7.48.0", {"start": v(112.49, 30.14) * mm, "mid": v(111.66, 33.08) * mm, "end": v(110.76, 35.99) * mm});
            skLineSegment(sketch, "E36.11.48.0", {"start": v(101.23, 27.12) * mm, "end": v(112.49, 30.14) * mm});
            skArc(sketch, "E36.3.49.0", {"start": v(97.84, 37.56) * mm, "mid": v(96.83, 40.1) * mm, "end": v(95.74, 42.63) * mm});
            skLineSegment(sketch, "E36.4.49.0", {"start": v(106.39, 47.37) * mm, "end": v(95.74, 42.63) * mm});
            skArc(sketch, "E36.7.49.0", {"start": v(108.72, 41.73) * mm, "mid": v(107.6, 44.57) * mm, "end": v(106.39, 47.37) * mm});
            skLineSegment(sketch, "E36.11.49.0", {"start": v(97.84, 37.56) * mm, "end": v(108.72, 41.73) * mm});
            skArc(sketch, "E36.3.50.0", {"start": v(93.38, 47.58) * mm, "mid": v(92.1, 50) * mm, "end": v(90.76, 52.4) * mm});
            skLineSegment(sketch, "E36.4.50.0", {"start": v(100.85, 58.23) * mm, "end": v(90.76, 52.4) * mm});
            skArc(sketch, "E36.7.50.0", {"start": v(103.76, 52.87) * mm, "mid": v(102.34, 55.57) * mm, "end": v(100.85, 58.23) * mm});
            skLineSegment(sketch, "E36.11.50.0", {"start": v(93.38, 47.58) * mm, "end": v(103.76, 52.87) * mm});
            skArc(sketch, "E36.3.51.0", {"start": v(87.9, 57.08) * mm, "mid": v(86.37, 59.36) * mm, "end": v(84.79, 61.6) * mm});
            skLineSegment(sketch, "E36.4.51.0", {"start": v(94.22, 68.45) * mm, "end": v(84.79, 61.6) * mm});
            skArc(sketch, "E36.7.51.0", {"start": v(97.67, 63.43) * mm, "mid": v(95.97, 65.96) * mm, "end": v(94.22, 68.45) * mm});
            skLineSegment(sketch, "E36.11.51.0", {"start": v(87.9, 57.08) * mm, "end": v(97.67, 63.43) * mm});
            skArc(sketch, "E36.3.52.0", {"start": v(81.45, 65.95) * mm, "mid": v(79.7, 68.06) * mm, "end": v(77.88, 70.13) * mm});
            skLineSegment(sketch, "E36.4.52.0", {"start": v(86.54, 77.92) * mm, "end": v(77.88, 70.13) * mm});
            skArc(sketch, "E36.7.52.0", {"start": v(90.5, 73.29) * mm, "mid": v(88.55, 75.63) * mm, "end": v(86.54, 77.92) * mm});
            skLineSegment(sketch, "E36.11.52.0", {"start": v(81.45, 65.95) * mm, "end": v(90.5, 73.29) * mm});
            skArc(sketch, "E36.3.53.0", {"start": v(74.1, 74.1) * mm, "mid": v(72.14, 76.02) * mm, "end": v(70.13, 77.88) * mm});
            skLineSegment(sketch, "E36.4.53.0", {"start": v(77.92, 86.54) * mm, "end": v(70.13, 77.88) * mm});
            skArc(sketch, "E36.7.53.0", {"start": v(82.35, 82.35) * mm, "mid": v(80.16, 84.47) * mm, "end": v(77.92, 86.54) * mm});
            skLineSegment(sketch, "E36.11.53.0", {"start": v(74.1, 74.1) * mm, "end": v(82.35, 82.35) * mm});
            skArc(sketch, "E36.3.54.0", {"start": v(65.95, 81.45) * mm, "mid": v(63.8, 83.15) * mm, "end": v(61.6, 84.79) * mm});
            skLineSegment(sketch, "E36.4.54.0", {"start": v(68.45, 94.22) * mm, "end": v(61.6, 84.79) * mm});
            skArc(sketch, "E36.7.54.0", {"start": v(73.29, 90.5) * mm, "mid": v(70.9, 92.4) * mm, "end": v(68.45, 94.22) * mm});
            skLineSegment(sketch, "E36.11.54.0", {"start": v(65.95, 81.45) * mm, "end": v(73.29, 90.5) * mm});
            skArc(sketch, "E36.3.55.0", {"start": v(57.08, 87.9) * mm, "mid": v(54.76, 89.36) * mm, "end": v(52.4, 90.76) * mm});
            skLineSegment(sketch, "E36.4.55.0", {"start": v(58.23, 100.85) * mm, "end": v(52.4, 90.76) * mm});
            skArc(sketch, "E36.7.55.0", {"start": v(63.43, 97.67) * mm, "mid": v(60.85, 99.3) * mm, "end": v(58.23, 100.85) * mm});
            skLineSegment(sketch, "E36.11.55.0", {"start": v(57.08, 87.9) * mm, "end": v(63.43, 97.67) * mm});
            skArc(sketch, "E36.3.56.0", {"start": v(47.58, 93.38) * mm, "mid": v(45.12, 94.6) * mm, "end": v(42.63, 95.74) * mm});
            skLineSegment(sketch, "E36.4.56.0", {"start": v(47.37, 106.39) * mm, "end": v(42.63, 95.74) * mm});
            skArc(sketch, "E36.7.56.0", {"start": v(52.87, 103.76) * mm, "mid": v(50.14, 105.11) * mm, "end": v(47.37, 106.39) * mm});
            skLineSegment(sketch, "E36.11.56.0", {"start": v(47.58, 93.38) * mm, "end": v(52.87, 103.76) * mm});
            skArc(sketch, "E36.3.57.0", {"start": v(37.56, 97.84) * mm, "mid": v(34.98, 98.8) * mm, "end": v(32.39, 99.67) * mm});
            skLineSegment(sketch, "E36.4.57.0", {"start": v(35.99, 110.76) * mm, "end": v(32.39, 99.67) * mm});
            skArc(sketch, "E36.7.57.0", {"start": v(41.73, 108.72) * mm, "mid": v(38.87, 109.78) * mm, "end": v(35.99, 110.76) * mm});
            skLineSegment(sketch, "E36.11.57.0", {"start": v(37.56, 97.84) * mm, "end": v(41.73, 108.72) * mm});
            skArc(sketch, "E36.3.58.0", {"start": v(27.12, 101.23) * mm, "mid": v(24.47, 101.9) * mm, "end": v(21.79, 102.51) * mm});
            skLineSegment(sketch, "E36.4.58.0", {"start": v(24.21, 113.91) * mm, "end": v(21.79, 102.51) * mm});
            skArc(sketch, "E36.7.58.0", {"start": v(30.14, 112.49) * mm, "mid": v(27.19, 113.24) * mm, "end": v(24.21, 113.91) * mm});
            skLineSegment(sketch, "E36.11.58.0", {"start": v(27.12, 101.23) * mm, "end": v(30.14, 112.49) * mm});
            skArc(sketch, "E36.3.59.0", {"start": v(16.4, 103.51) * mm, "mid": v(13.68, 103.9) * mm, "end": v(10.95, 104.23) * mm});
            skLineSegment(sketch, "E36.4.59.0", {"start": v(12.17, 115.82) * mm, "end": v(10.95, 104.23) * mm});
            skArc(sketch, "E36.7.59.0", {"start": v(18.22, 115.02) * mm, "mid": v(15.2, 115.46) * mm, "end": v(12.17, 115.82) * mm});
            skLineSegment(sketch, "E36.11.59.0", {"start": v(16.4, 103.51) * mm, "end": v(18.22, 115.02) * mm});
            skSolve(sketch);
        }
        {
            var Q0;
            Q0=qSketchRegion(id+"F4",true);
            extrude(context, id + "F5", {"entities" : qUnion([Q0]), "operationType" : NewBodyOperationType.REMOVE, "oppositeDirection" : true, "depth" : 25 * mm, "offsetDistance" : 25 * mm});
        }
        {
            var Q0;
            Q0=makeQuery(id+"F3.boolean.opBoolean","MERGE",FACE,{"derivedFrom":[makeQuery(id+"F1.opExtrude","CAP_FACE",FACE,{"disambiguationData":[OSD([sQuery(id+"F0.wireOp",EDGE,"E6"),sQuery(id+"F0.wireOp",EDGE,"E7"),sQuery(id+"F0.wireOp",EDGE,"E8"),sQuery(id+"F0.wireOp",EDGE,"E9"),sQuery(id+"F0.wireOp",EDGE,"E10.MirrorCS"),sQuery(id+"F0.wireOp",EDGE,"E11.MirrorCS"),sQuery(id+"F0.wireOp",EDGE,"E12.MirrorCS"),sQuery(id+"F0.wireOp",EDGE,"E13.MirrorCS"),sQuery(id+"F0.wireOp",EDGE,"E14.MirrorCS"),sQuery(id+"F0.wireOp",EDGE,"E15.MirrorCS"),sQuery(id+"F0.wireOp",EDGE,"E16.MirrorCS"),sQuery(id+"F0.wireOp",EDGE,"E17.MirrorCS"),sQuery(id+"F0.wireOp",EDGE,"E18.MirrorCS"),sQuery(id+"F0.wireOp",EDGE,"E19.MirrorCS"),sQuery(id+"F0.wireOp",EDGE,"E20.MirrorCS"),sQuery(id+"F0.wireOp",EDGE,"E21.MirrorCS"),sQuery(id+"F0.wireOp",EDGE,"E25")])],"isStart":false}),makeQuery(id+"F3.opExtrude","CAP_FACE",FACE,{"disambiguationData":[OSD([sQuery(id+"F2.wireOp",EDGE,"E26"),sQuery(id+"F2.wireOp",EDGE,"E27")])],"isStart":true})]});
            var sketch = newSketch(context, id + "F6", { "sketchPlane" : qUnion([Q0])});
            skCircle(sketch, "E37", {"center": v(0, 0) * mm, "radius": 95 * mm});
            skSolve(sketch);
        }
        {
            var Q0;
            Q0 = qSketchRegion(id + "F6", true);
            extrude(context, id + "F7", {"entities" : qUnion([Q0]), "operationType" : NewBodyOperationType.REMOVE, "oppositeDirection" : true, "depth" : 25 * mm, "offsetDistance" : 25 * mm});
        }
    });
